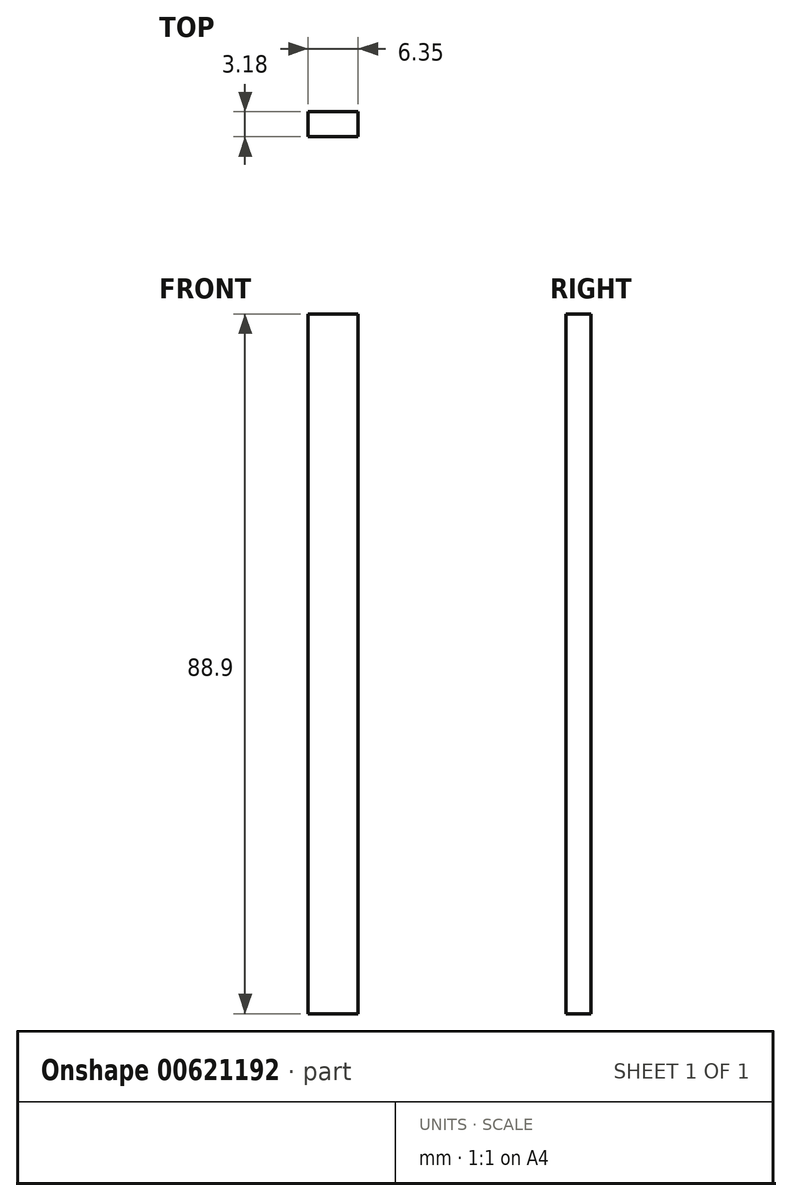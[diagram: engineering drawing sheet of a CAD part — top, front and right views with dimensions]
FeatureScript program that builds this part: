
annotation { "Feature Type Name" : "Feature", "Feature Type Description" : "" }
export const myFeature = defineFeature(function(context is Context, id is Id, definition is map)
    precondition{}
    {
        {
            var Q0;
            Q0=qCreatedBy(makeId("Right.planeOp"),FACE);
            var sketch = newSketch(context, id + "F0", { "sketchPlane" : qUnion([Q0])});
            skLineSegment(sketch, "E0.bottom", {"start": v(6.35, 0) * mm, "end": v(50.8, 0) * mm});
            skLineSegment(sketch, "E0.top", {"start": v(0, -177.8) * mm, "end": v(50.8, -177.8) * mm});
            skLineSegment(sketch, "E0.left", {"start": v(0, -6.35) * mm, "end": v(0, -177.8) * mm});
            skLineSegment(sketch, "E0.right", {"start": v(50.8, 0) * mm, "end": v(50.8, -177.8) * mm});
            skPoint(sketch, "E1.visualSharp", {"position": v(0, 0) * mm});
            skArc(sketch, "E1.filletArc", {"start": v(6.35, 0) * mm, "mid": v(1.86, -1.86) * mm, "end": v(0, -6.35) * mm});
            skLineSegment(sketch, "E2.bottom", {"start": v(50.8, 0) * mm, "end": v(47.62, 0) * mm});
            skLineSegment(sketch, "E2.top", {"start": v(50.8, -88.9) * mm, "end": v(47.63, -88.9) * mm});
            skLineSegment(sketch, "E2.left", {"start": v(50.8, 0) * mm, "end": v(50.8, -88.9) * mm});
            skLineSegment(sketch, "E2.right", {"start": v(47.62, 0) * mm, "end": v(47.63, -88.9) * mm});
            skSolve(sketch);
        }
        {
            var Q0;
            Q0=makeQuery(id+"F0.imprint","IMPRINT",FACE,{"disambiguationData":[TD([[makeQuery(id+"F0.imprint","IMPRINT",EDGE,{"derivedFrom":sQuery(id+"F0.wireOp",EDGE,"E0.bottom")}),-1.0]])]});
            extrude(context, id + "F1", {"entities" : qUnion([Q0]), "depth" : 6.35 * mm, "offsetDistance" : 25.4 * mm});
        }
    });
